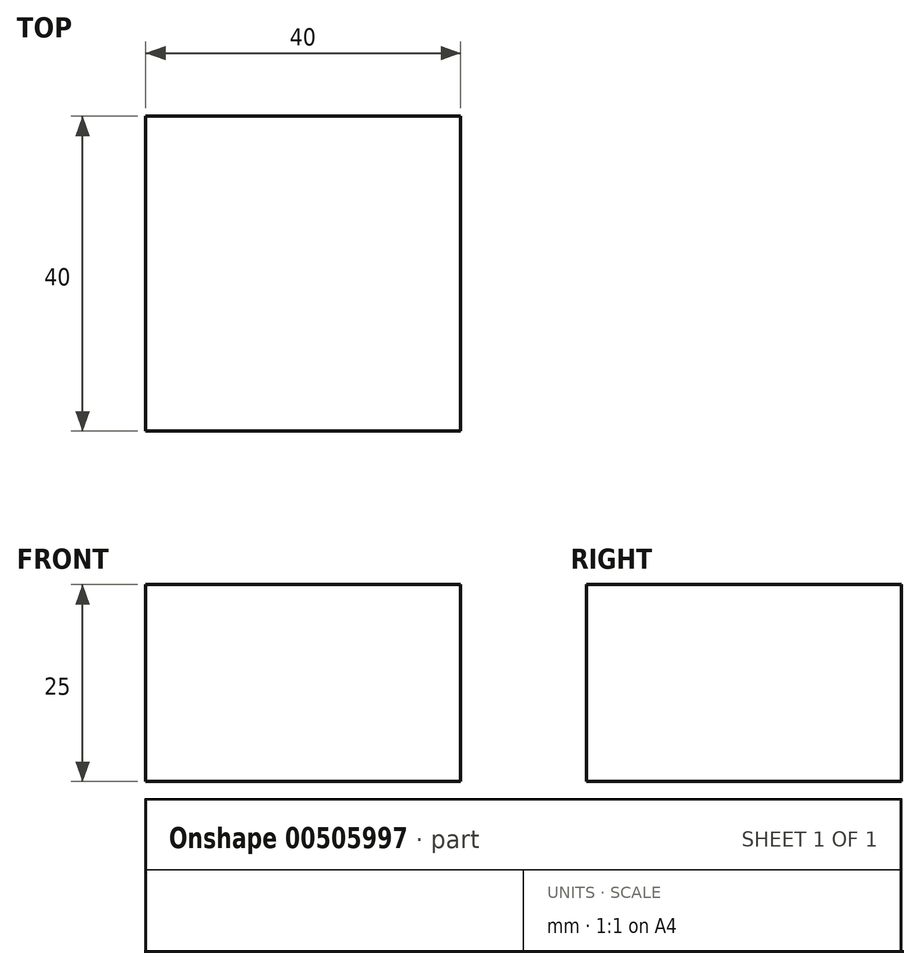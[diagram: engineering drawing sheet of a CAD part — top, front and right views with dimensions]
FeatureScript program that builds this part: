
annotation { "Feature Type Name" : "Feature", "Feature Type Description" : "" }
export const myFeature = defineFeature(function(context is Context, id is Id, definition is map)
    precondition{}
    {
        {
            var Q0;
            Q0=qCreatedBy(makeId("Top.planeOp"),FACE);
            var sketch = newSketch(context, id + "F0", { "sketchPlane" : qUnion([Q0])});
            skLineSegment(sketch, "E0.bottom", {"start": v(0, 0) * mm, "end": v(40, 0) * mm});
            skLineSegment(sketch, "E0.top", {"start": v(0, 40) * mm, "end": v(40, 40) * mm});
            skLineSegment(sketch, "E0.left", {"start": v(0, 0) * mm, "end": v(0, 40) * mm});
            skLineSegment(sketch, "E0.right", {"start": v(40, 0) * mm, "end": v(40, 40) * mm});
            skSolve(sketch);
        }
        {
            var Q0;
            Q0=makeQuery(id+"F0.imprint","IMPRINT",FACE,{"disambiguationData":[TD([[makeQuery(id+"F0.imprint","IMPRINT",EDGE,{"derivedFrom":sQuery(id+"F0.wireOp",EDGE,"E0.bottom")}),1.0]])]});
            extrude(context, id + "F1", {"entities" : qUnion([Q0]), "depth" : 25 * mm});
        }
    });
